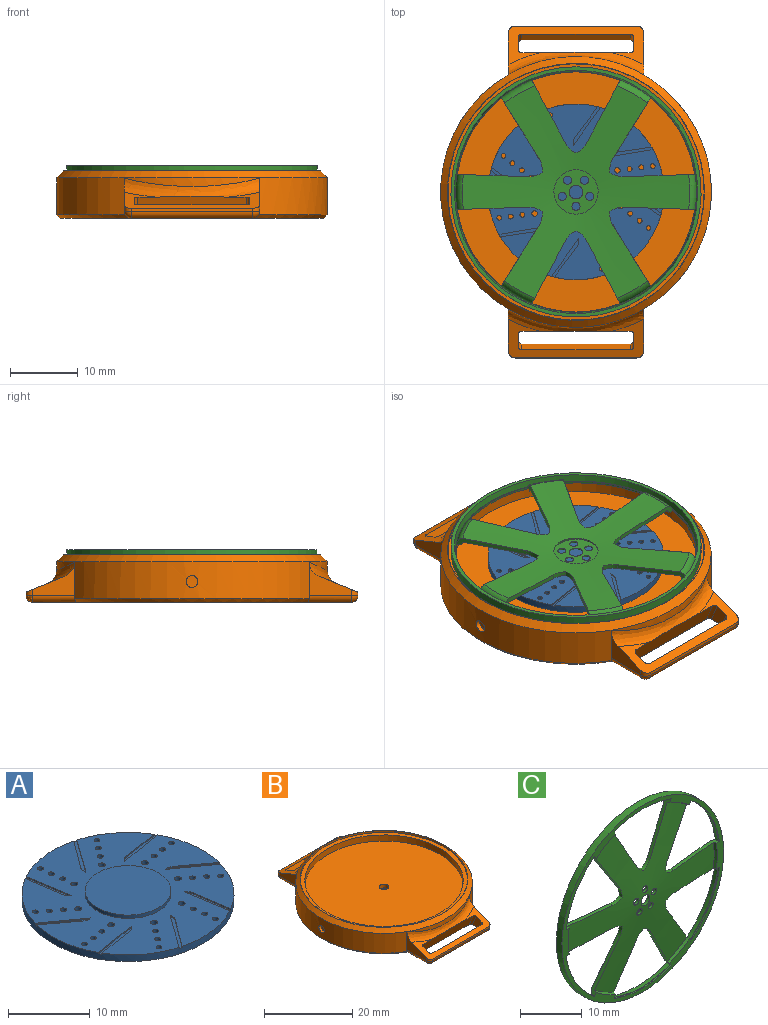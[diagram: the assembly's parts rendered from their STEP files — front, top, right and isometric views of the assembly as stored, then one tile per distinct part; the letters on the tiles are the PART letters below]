
ASSEMBLY  parts=3 mates=2
PART A: 69 faces, bbox 26x26x1.5 mm
  f0: cylinder r=0.41mm len=1mm, axis (0,0,1), area 2.6mm2, adj f57,f58
  f1: cylinder r=0.35mm len=1mm, axis (0,0,1), area 2.2mm2, adj f57,f58
  f2: cylinder r=0.36mm len=1mm, axis (0,0,1), area 2.3mm2, adj f57,f58
  f3: cylinder r=0.37mm len=1mm, axis (0,0,1), area 2.3mm2, adj f57,f58
  f4: cylinder r=0.41mm len=1mm, axis (0,0,1), area 2.6mm2, adj f57,f58
  f5: cylinder r=0.35mm len=1mm, axis (0,0,1), area 2.2mm2, adj f57,f58
  f6: cylinder r=0.36mm len=1mm, axis (0,0,1), area 2.3mm2, adj f57,f58
  f7: cylinder r=0.37mm len=1mm, axis (0,0,1), area 2.3mm2, adj f57,f58
  f8: cylinder r=0.41mm len=1mm, axis (0,0,1), area 2.6mm2, adj f57,f58
  f9: cylinder r=0.35mm len=1mm, axis (0,0,1), area 2.2mm2, adj f57,f58
  f10: cylinder r=0.36mm len=1mm, axis (0,0,1), area 2.3mm2, adj f57,f58
  f11: cylinder r=0.37mm len=1mm, axis (0,0,1), area 2.3mm2, adj f57,f58
  f12: cylinder r=0.41mm len=1mm, axis (0,0,1), area 2.6mm2, adj f57,f58
  f13: cylinder r=0.35mm len=1mm, axis (0,0,1), area 2.2mm2, adj f57,f58
  f14: cylinder r=0.36mm len=1mm, axis (0,0,1), area 2.3mm2, adj f57,f58
  f15: cylinder r=0.37mm len=1mm, axis (0,0,1), area 2.3mm2, adj f57,f58
  f16: cylinder r=0.41mm len=1mm, axis (0,0,1), area 2.6mm2, adj f57,f58
  f17: cylinder r=0.35mm len=1mm, axis (0,0,1), area 2.2mm2, adj f57,f58
  f18: cylinder r=0.36mm len=1mm, axis (0,0,1), area 2.3mm2, adj f57,f58
  f19: cylinder r=0.37mm len=1mm, axis (0,0,1), area 2.3mm2, adj f57,f58
  f20: cylinder r=0.41mm len=1mm, axis (0,0,1), area 2.6mm2, adj f57,f58
  f21: cylinder r=0.35mm len=1mm, axis (0,0,1), area 2.2mm2, adj f57,f58
  f22: cylinder r=0.36mm len=1mm, axis (0,0,1), area 2.3mm2, adj f57,f58
  f23: cylinder r=0.37mm len=1mm, axis (0,0,1), area 2.3mm2, adj f57,f58
  f24: cylinder r=0.41mm len=1mm, axis (0,0,1), area 2.6mm2, adj f57,f58
  f25: cylinder r=0.35mm len=1mm, axis (0,0,1), area 2.2mm2, adj f57,f58
  f26: cylinder r=0.36mm len=1mm, axis (0,0,1), area 2.3mm2, adj f57,f58
  f27: cylinder r=0.37mm len=1mm, axis (0,0,1), area 2.3mm2, adj f57,f58
  f28: plane 6.79x1.11mm, normal (-0.16,0.99,0), area 1.2mm2, adj f30,f31,f56,f57
  f29: plane 5.62x0.83mm, normal (0.15,-0.99,0), area 1mm2, adj f30,f31,f56,f57
  f30: cylinder r=1.33mm len=0.95mm, axis (0,0,1), area 0.2mm2, adj f28,f29,f31,f57
  f31: plane 6.79x1.48mm, normal (0,0,1), area 2.9mm2, adj f28,f29,f30,f56
  f32: plane 5.59x4.01mm, normal (0.58,0.81,0), area 1.2mm2, adj f34,f35,f56,f57
  f33: plane 4.57x3.39mm, normal (-0.6,-0.8,0), area 1mm2, adj f34,f35,f56,f57
  f34: cylinder r=1.33mm len=1.13mm, axis (0,0,1), area 0.2mm2, adj f32,f33,f35,f57
  f35: plane 5.7x4.06mm, normal (0,0,1), area 2.9mm2, adj f32,f33,f34,f56
  f36: plane 6.79x1.11mm, normal (0.99,0.16,0), area 1.2mm2, adj f38,f39,f56,f57
  f37: plane 5.62x0.83mm, normal (-0.99,-0.15,0), area 1mm2, adj f38,f39,f56,f57
  f38: cylinder r=1.33mm len=0.95mm, axis (0,0,1), area 0.2mm2, adj f36,f37,f39,f57
  f39: plane 6.79x1.48mm, normal (0,0,1), area 2.9mm2, adj f36,f37,f38,f56
  f40: plane 5.59x4.01mm, normal (0.81,-0.58,0), area 1.2mm2, adj f42,f43,f56,f57
  f41: plane 4.57x3.39mm, normal (-0.8,0.6,0), area 1mm2, adj f42,f43,f56,f57
  f42: cylinder r=1.33mm len=1.13mm, axis (0,0,1), area 0.2mm2, adj f40,f41,f43,f57
  f43: plane 5.7x4.06mm, normal (0,0,1), area 2.9mm2, adj f40,f41,f42,f56
  f44: plane 6.79x1.11mm, normal (0.16,-0.99,0), area 1.2mm2, adj f46,f47,f56,f57
  f45: plane 5.62x0.83mm, normal (-0.15,0.99,0), area 1mm2, adj f46,f47,f56,f57
  f46: cylinder r=1.33mm len=0.95mm, axis (0,0,1), area 0.2mm2, adj f44,f45,f47,f57
  f47: plane 6.79x1.48mm, normal (0,0,1), area 2.9mm2, adj f44,f45,f46,f56
  f48: plane 5.59x4.01mm, normal (-0.58,-0.81,0), area 1.2mm2, adj f50,f51,f56,f57
  f49: plane 4.57x3.39mm, normal (0.6,0.8,0), area 1mm2, adj f50,f51,f56,f57
  f50: cylinder r=1.33mm len=1.13mm, axis (0,0,1), area 0.2mm2, adj f48,f49,f51,f57
  f51: plane 5.7x4.06mm, normal (0,0,1), area 2.9mm2, adj f48,f49,f50,f56
  f52: plane 6.79x1.11mm, normal (-0.99,-0.16,0), area 1.2mm2, adj f54,f55,f56,f57
  f53: plane 5.62x0.83mm, normal (0.99,0.15,0), area 1mm2, adj f54,f55,f56,f57
  f54: cylinder r=1.33mm len=0.95mm, axis (0,0,1), area 0.2mm2, adj f52,f53,f55,f57
  f55: plane 6.79x1.48mm, normal (0,0,1), area 2.9mm2, adj f52,f53,f54,f56
  f56: cylinder r=13mm len=26mm, axis (0,0,-1), area 81.1mm2, adj f28,f29,f31,f32,f33,f35,f36,f37
  f57: plane 26x26mm, normal (0,0,1), area 407mm2, adj f0,f1,f2,f3,f4,f5,f6,f7
  f58: plane 26x26mm, normal (0,0,-1), area 516.8mm2, adj f0,f1,f2,f3,f4,f5,f6,f7
  f59: cylinder r=5.26mm len=10.51mm, axis (0,0,-1), area 16.5mm2, adj f57,f60
  f60: plane 10.51x10.51mm, normal (0,0,1), area 86.8mm2, adj f59
  f61: plane 5.7x4.06mm, normal (0,0,1), area 2.9mm2, adj f56,f62,f63,f64
  f62: plane 5.59x4.01mm, normal (-0.81,0.58,0), area 1.2mm2, adj f56,f57,f61,f64
  f63: plane 4.57x3.39mm, normal (0.8,-0.6,0), area 1mm2, adj f56,f57,f61,f64
  f64: cylinder r=1.33mm len=1.13mm, axis (0,0,1), area 0.2mm2, adj f57,f61,f62,f63
  f65: cylinder r=0.37mm len=1mm, axis (0,0,1), area 2.3mm2, adj f57,f58
  f66: cylinder r=0.36mm len=1mm, axis (0,0,1), area 2.3mm2, adj f57,f58
  f67: cylinder r=0.35mm len=1mm, axis (0,0,1), area 2.2mm2, adj f57,f58
  f68: cylinder r=0.41mm len=1mm, axis (0,0,1), area 2.6mm2, adj f57,f58
PART B: 56 faces, bbox 41.5x50.5x8.6 mm
  f0: bspline ~22x3.91mm, area 50mm2, adj f1,f13,f14,f16,f40
  f1: cylinder r=20mm len=40mm, axis (0,0,-1), area 495.5mm2, adj f0,f2,f3,f4,f5,f8,f13,f14
  f2: cylinder r=20mm len=0.5mm, axis (0,0,-1), area 0mm2, adj f1,f4,f44
  f3: cone r=20mm half-angle=45deg, axis (0,0,1), area 30mm2, adj f1,f7,f47,f50
  f4: cone r=20mm half-angle=45deg, axis (0,0,1), area 29.7mm2, adj f1,f2,f7,f44,f53
  f5: cylinder r=0.88mm len=1.77mm, axis (1,0,0), area 4mm2, adj f1,f18
  f6: plane 38x38mm, normal (0,0,1), area 7mm2, adj f8,f9
  f7: plane 47.17x39.09mm, normal (0,0,-1), area 231.1mm2, adj f3,f4,f17,f23,f25,f26,f27,f28
  f8: cone r=19mm half-angle=45deg, axis (0,0,-1), area 173.3mm2, adj f1,f6
  f9: cylinder r=18.94mm len=37.88mm, axis (0,0,1), area 59.5mm2, adj f6,f10
  f10: plane 37.88x37.88mm, normal (0,0,1), area 115.7mm2, adj f9,f11
  f11: cylinder r=17.94mm len=35.89mm, axis (0,0,-1), area 191.7mm2, adj f10,f12
  f12: plane 35.89x35.89mm, normal (0,0,1), area 1007.7mm2, adj f11,f43
  f13: plane 6.41x5.11mm, normal (-1,0,0), area 14mm2, adj f0,f1,f16,f53,f55
  f14: plane 6.41x5.12mm, normal (1,0,0), area 14mm2, adj f0,f1,f16,f50,f52
  f15: plane 18x0.49mm, normal (0,1,0), area 8.8mm2, adj f16,f17,f52,f55
  f16: plane 20.17x5.89mm, normal (0,0.38,0.92), area 42.5mm2, adj f0,f13,f14,f15,f33,f34,f35,f36
  f17: cylinder r=1mm len=18mm, axis (-1,0,0), area 28.3mm2, adj f7,f15,f51,f54
  f18: cylinder r=19.27mm len=1.77mm, axis (0,0,-1), area 2.5mm2, adj f5
  f19: plane 18x0.49mm, normal (0,-1,0), area 8.8mm2, adj f22,f23,f46,f49
  f20: plane 6.41x5.11mm, normal (1,0,0), area 14mm2, adj f1,f22,f24,f47,f49
  f21: plane 6.41x5.12mm, normal (-1,0,0), area 14mm2, adj f1,f22,f24,f44,f46
  f22: plane 20.17x5.89mm, normal (0,-0.38,0.92), area 42.5mm2, adj f19,f20,f21,f24,f25,f26,f27,f28
  f23: cylinder r=1mm len=18mm, axis (1,0,0), area 28.3mm2, adj f7,f19,f45,f48
  f24: bspline ~22x3.91mm, area 50mm2, adj f1,f20,f21,f22,f32
  f25: cylinder r=0.5mm len=3.32mm, axis (0,-0.38,0.92), area 2.6mm2, adj f7,f22,f26,f32
  f26: plane 3.07x2.94mm, normal (1,0,0), area 5.5mm2, adj f7,f22,f25,f27
  f27: cylinder r=0.5mm len=2.37mm, axis (0,-0.38,0.92), area 1.8mm2, adj f7,f22,f26,f28
  f28: plane 15.99x1.98mm, normal (0,0.92,0.38), area 34.3mm2, adj f7,f22,f27,f29
  f29: cylinder r=0.5mm len=2.37mm, axis (0,-0.38,0.92), area 1.8mm2, adj f7,f22,f28,f30
  f30: plane 3.07x2.94mm, normal (-1,0,0), area 5.5mm2, adj f7,f22,f29,f31
  f31: cylinder r=0.5mm len=3.32mm, axis (0,-0.38,0.92), area 2.6mm2, adj f7,f22,f30,f32
  f32: plane 17.44x4.71mm, normal (0,-0.92,-0.38), area 54.9mm2, adj f7,f22,f24,f25,f31
  f33: plane 3.07x2.94mm, normal (-1,0,0), area 5.5mm2, adj f7,f16,f34,f39
  f34: cylinder r=0.5mm len=2.37mm, axis (0,0.38,0.92), area 1.8mm2, adj f7,f16,f33,f35
  f35: plane 15.99x1.98mm, normal (0,-0.92,0.38), area 34.3mm2, adj f7,f16,f34,f36
  f36: cylinder r=0.5mm len=2.37mm, axis (0,0.38,0.92), area 1.8mm2, adj f7,f16,f35,f37
  f37: plane 3.07x2.94mm, normal (1,0,0), area 5.5mm2, adj f7,f16,f36,f38
  f38: cylinder r=0.5mm len=3.32mm, axis (0,0.38,0.92), area 2.6mm2, adj f7,f16,f37,f40
  f39: cylinder r=0.5mm len=3.32mm, axis (0,0.38,0.92), area 2.6mm2, adj f7,f16,f33,f40
  f40: plane 17.44x4.71mm, normal (0,0.92,-0.38), area 54.9mm2, adj f0,f7,f16,f38,f39
  f41: cylinder r=18.06mm len=36.12mm, axis (0,0,-1), area 419.9mm2, adj f7,f42
  f42: plane 36.12x36.12mm, normal (0,0,-1), area 1021.2mm2, adj f41,f43
  f43: cylinder r=1.09mm len=2.17mm, axis (0,0,1), area 7.5mm2, adj f12,f42
  f44: cylinder r=1mm len=6.24mm, axis (0,-1,0), area 9.7mm2, adj f2,f4,f7,f21,f45
  f45: sphere r=1mm, area 1.6mm2, adj f23,f44,f46
  f46: cylinder r=1mm len=1mm, axis (0,0,1), area 1.1mm2, adj f19,f21,f22,f45
  f47: cylinder r=1mm len=6.24mm, axis (0,1,0), area 9.7mm2, adj f1,f3,f7,f20,f48
  f48: sphere r=1mm, area 1.6mm2, adj f23,f47,f49
  f49: cylinder r=1mm len=1mm, axis (0,0,-1), area 1.1mm2, adj f19,f20,f22,f48
  f50: cylinder r=1mm len=6.24mm, axis (0,1,0), area 9.7mm2, adj f1,f3,f7,f14,f51
  f51: sphere r=1mm, area 1mm2, adj f17,f50,f52
  f52: cylinder r=1mm len=1mm, axis (0,0,-1), area 1.1mm2, adj f14,f15,f16,f51
  f53: cylinder r=1mm len=6.24mm, axis (0,-1,0), area 9.7mm2, adj f1,f4,f7,f13,f54
  f54: sphere r=1mm, area 1mm2, adj f17,f53,f55
  f55: cylinder r=1mm len=1mm, axis (0,0,1), area 1.1mm2, adj f13,f15,f16,f54
PART C: 63 faces, bbox 39.3x2.6x39.3 mm
  f0: torus R=16.46mm, axis (0,-1,0), area 7.8mm2, adj f5,f6,f43,f45,f54,f55
  f1: cone r=17.04mm half-angle=20.1deg, axis (0,-1,0), area 2.9mm2, adj f6,f41,f49,f54
  f2: cylinder r=18.91mm len=6.29mm, axis (0,1,0), area 1.8mm2, adj f3,f5,f8,f41,f43
  f3: plane 11.33x2.12mm, normal (-0.03,0,1), area 7.4mm2, adj f2,f4,f8,f9,f41,f45,f49
  f4: cylinder r=3.06mm len=1.97mm, axis (0,1,0), area 1.4mm2, adj f3,f7,f45,f49
  f5: cylinder r=18.91mm len=5.03mm, axis (0,1,0), area 1.8mm2, adj f0,f2,f6,f41,f43
  f6: plane 9.75x6.34mm, normal (0.85,0,-0.53), area 7.4mm2, adj f0,f1,f5,f7,f41,f45,f49
  f7: cylinder r=3.06mm len=2.03mm, axis (0,1,0), area 1.4mm2, adj f4,f6,f45,f49
  f8: torus R=16.46mm, axis (0,-1,0), area 7.8mm2, adj f2,f3,f13,f14,f43,f45
  f9: cone r=17.04mm half-angle=20.1deg, axis (0,-1,0), area 2.9mm2, adj f3,f14,f41,f49
  f10: cylinder r=18.91mm len=5.03mm, axis (0,1,0), area 1.8mm2, adj f11,f13,f16,f41,f43
  f11: plane 9.75x6.34mm, normal (0.85,0,0.53), area 7.4mm2, adj f10,f12,f16,f17,f41,f45,f49
  f12: cylinder r=3.06mm len=2.03mm, axis (0,1,0), area 1.4mm2, adj f11,f15,f45,f49
  f13: cylinder r=18.91mm len=6.29mm, axis (0,1,0), area 1.8mm2, adj f8,f10,f14,f41,f43
  f14: plane 11.33x2.12mm, normal (-0.03,0,-1), area 7.4mm2, adj f8,f9,f13,f15,f41,f45,f49
  f15: cylinder r=3.06mm len=1.97mm, axis (0,1,0), area 1.4mm2, adj f12,f14,f45,f49
  f16: torus R=16.46mm, axis (0,-1,0), area 7.8mm2, adj f10,f11,f21,f22,f43,f45
  f17: cone r=17.04mm half-angle=20.1deg, axis (0,-1,0), area 2.9mm2, adj f11,f22,f41,f49
  f18: cylinder r=18.91mm len=6.54mm, axis (0,1,0), area 1.8mm2, adj f19,f21,f24,f41,f43
  f19: plane 10.08x5.76mm, normal (0.88,0,-0.47), area 7.4mm2, adj f18,f20,f24,f25,f41,f45,f49
  f20: cylinder r=3.06mm len=1.54mm, axis (0,1,0), area 1.4mm2, adj f19,f23,f45,f49
  f21: cylinder r=18.91mm len=6.54mm, axis (0,1,0), area 1.8mm2, adj f16,f18,f22,f41,f43
  f22: plane 10.08x5.76mm, normal (-0.88,0,-0.47), area 7.4mm2, adj f16,f17,f21,f23,f41,f45,f49
  f23: cylinder r=3.06mm len=1.54mm, axis (0,1,0), area 1.4mm2, adj f20,f22,f45,f49
  f24: torus R=16.46mm, axis (0,-1,0), area 7.8mm2, adj f18,f19,f29,f30,f43,f45
  f25: cone r=17.04mm half-angle=20.1deg, axis (0,-1,0), area 2.9mm2, adj f19,f30,f41,f49
  f26: cylinder r=18.91mm len=6.29mm, axis (0,1,0), area 1.8mm2, adj f27,f29,f32,f41,f43
  f27: plane 11.33x2.12mm, normal (0.03,0,-1), area 7.4mm2, adj f26,f28,f32,f33,f41,f45,f49
  f28: cylinder r=3.06mm len=1.97mm, axis (0,1,0), area 1.4mm2, adj f27,f31,f45,f49
  f29: cylinder r=18.91mm len=5.03mm, axis (0,1,0), area 1.8mm2, adj f24,f26,f30,f41,f43
  f30: plane 9.75x6.34mm, normal (-0.85,0,0.53), area 7.4mm2, adj f24,f25,f29,f31,f41,f45,f49
  f31: cylinder r=3.06mm len=2.03mm, axis (0,1,0), area 1.4mm2, adj f28,f30,f45,f49
  f32: torus R=16.46mm, axis (0,-1,0), area 7.8mm2, adj f26,f27,f37,f38,f43,f45
  f33: cone r=17.04mm half-angle=20.1deg, axis (0,-1,0), area 2.9mm2, adj f27,f38,f41,f49
  f34: cylinder r=18.91mm len=5.03mm, axis (0,1,0), area 1.8mm2, adj f35,f37,f40,f41,f43
  f35: plane 9.75x6.34mm, normal (-0.85,0,-0.53), area 7.4mm2, adj f34,f36,f40,f41,f42,f45,f49
  f36: cylinder r=3.06mm len=2.03mm, axis (0,1,0), area 1.4mm2, adj f35,f39,f45,f49
  f37: cylinder r=18.91mm len=6.29mm, axis (0,1,0), area 1.8mm2, adj f32,f34,f38,f41,f43
  f38: plane 11.33x2.12mm, normal (0.03,0,1), area 7.4mm2, adj f32,f33,f37,f39,f41,f45,f49
  f39: cylinder r=3.06mm len=1.97mm, axis (0,1,0), area 1.4mm2, adj f36,f38,f45,f49
  f40: torus R=16.46mm, axis (0,-1,0), area 7.8mm2, adj f34,f35,f43,f45,f51,f52
  f41: plane 37x37mm, normal (0,-1,0), area 108.3mm2, adj f1,f2,f3,f5,f6,f9,f10,f11
  f42: cone r=17.04mm half-angle=20.1deg, axis (0,-1,0), area 2.9mm2, adj f35,f41,f49,f52
  f43: plane 35.71x35.71mm, normal (0,1,0), area 11.3mm2, adj f0,f2,f5,f8,f10,f13,f16,f18
  f44: cone r=3.29mm half-angle=4.1deg, axis (0,-1,0), area 4.8mm2, adj f45,f50
  f45: cone r=3.27mm half-angle=85.9deg, axis (0,1,0), area 429.9mm2, adj f0,f3,f4,f6,f7,f8,f11,f12
  f46: cone r=17.86mm half-angle=7.2deg, axis (0,1,0), area 114.8mm2, adj f43,f47
  f47: plane 37x37mm, normal (0,1,0), area 59.2mm2, adj f46,f48
  f48: cylinder r=18.5mm len=37mm, axis (0,-1,0), area 148.4mm2, adj f41,f47
  f49: cone r=16.85mm half-angle=85.9deg, axis (0,1,0), area 420.9mm2, adj f1,f3,f4,f6,f7,f9,f11,f12
  f50: plane 6.57x6.57mm, normal (0,1,0), area 25.1mm2, adj f44,f57,f58,f59,f60,f61,f62
  f51: cylinder r=18.91mm len=6.54mm, axis (0,1,0), area 1.8mm2, adj f40,f41,f43,f52,f55
  f52: plane 10.08x5.76mm, normal (0.88,0,0.47), area 7.4mm2, adj f40,f41,f42,f45,f49,f51,f53
  f53: cylinder r=3.06mm len=1.54mm, axis (0,1,0), area 1.4mm2, adj f45,f49,f52,f56
  f54: plane 10.08x5.76mm, normal (-0.88,0,0.47), area 7.4mm2, adj f0,f1,f41,f45,f49,f55,f56
  f55: cylinder r=18.91mm len=6.54mm, axis (0,1,0), area 1.8mm2, adj f0,f41,f43,f51,f54
  f56: cylinder r=3.06mm len=1.54mm, axis (0,1,0), area 1.4mm2, adj f45,f49,f53,f54
  f57: cylinder r=1.02mm len=2.04mm, axis (0,1,0), area 3.9mm2, adj f49,f50
  f58: cylinder r=0.6mm len=1.2mm, axis (0,1,0), area 2mm2, adj f49,f50
  f59: cylinder r=0.6mm len=1.2mm, axis (0,1,0), area 2mm2, adj f49,f50
  f60: cylinder r=0.6mm len=1.2mm, axis (0,1,0), area 2mm2, adj f49,f50
  f61: cylinder r=0.6mm len=1.2mm, axis (0,1,0), area 1.9mm2, adj f49,f50
  f62: cylinder r=0.6mm len=1.2mm, axis (0,1,0), area 2mm2, adj f49,f50
PLACE A t=(-8.14,-5.71,16.51)mm
PLACE B t=(-8.14,-5.71,11.71)mm
PLACE C rot(axis=(1,0,0),90deg) t=(-8.14,-5.71,18.21)mm
MATE fastened A.f56 <-> B.f11  axis (0,0,-1) through (-8.14,-5.71,16.51)mm
MATE fastened C.f0 <-> B.f1  axis (0,0,-1) through (-8.14,-5.71,18.21)mm
